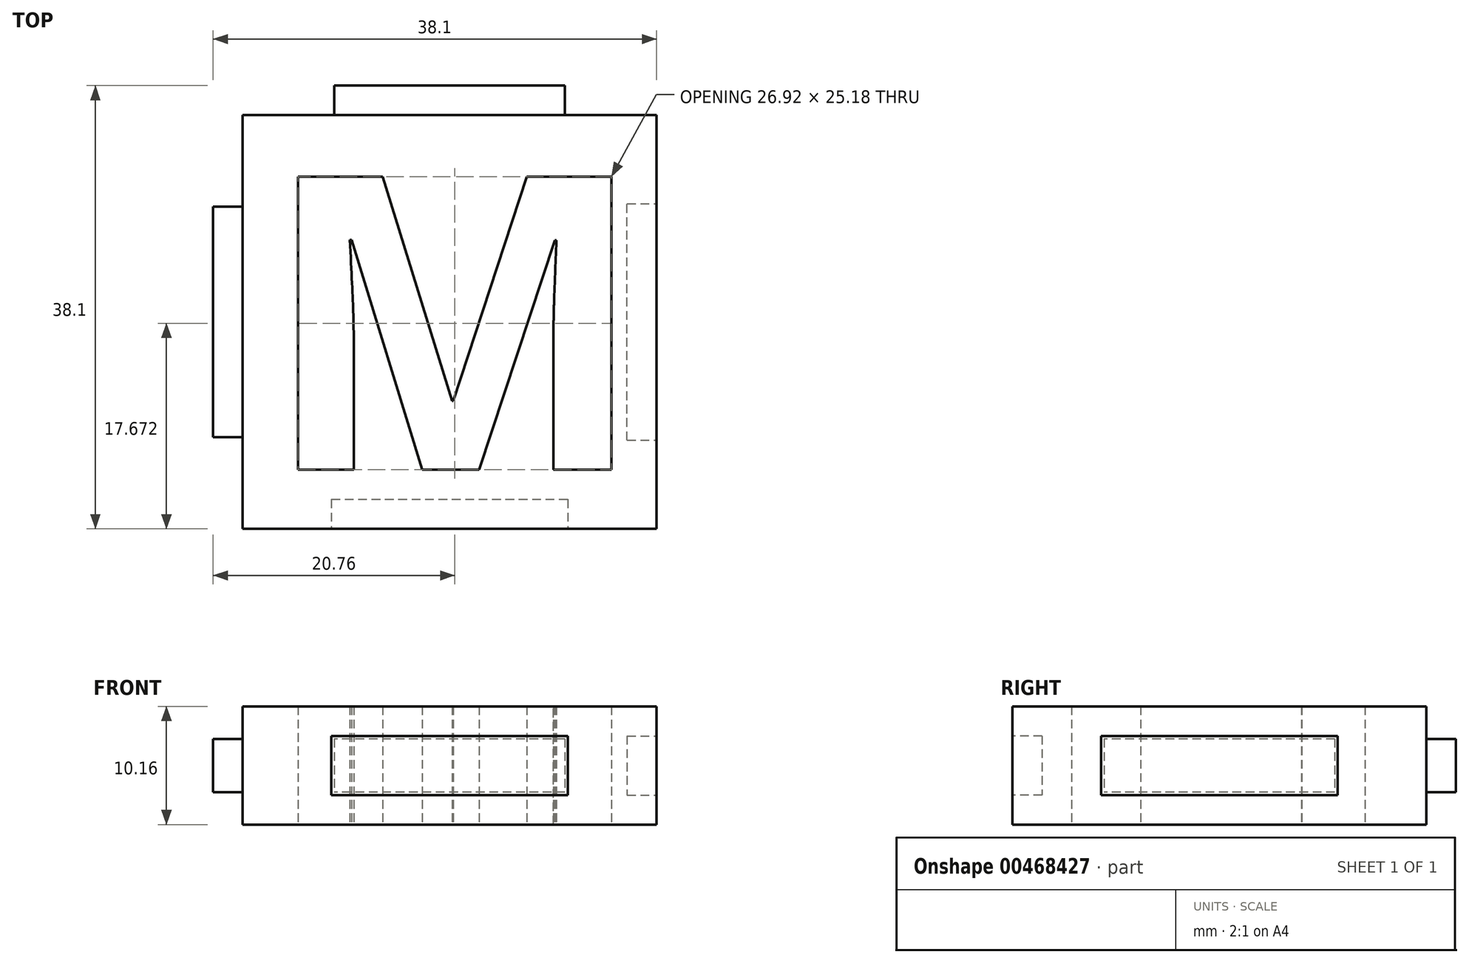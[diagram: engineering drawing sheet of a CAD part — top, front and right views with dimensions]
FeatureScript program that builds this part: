
annotation { "Feature Type Name" : "Feature", "Feature Type Description" : "" }
export const myFeature = defineFeature(function(context is Context, id is Id, definition is map)
    precondition{}
    {
        {
            var Q0;
            Q0=qCreatedBy(makeId("Top.planeOp"),FACE);
            var sketch = newSketch(context, id + "F0", { "sketchPlane" : qUnion([Q0])});
            skLineSegment(sketch, "E0.bottom", {"start": v(-17.78, 17.78) * mm, "end": v(17.78, 17.78) * mm});
            skLineSegment(sketch, "E0.top", {"start": v(-17.78, -17.78) * mm, "end": v(17.78, -17.78) * mm});
            skLineSegment(sketch, "E0.left", {"start": v(-17.78, 17.78) * mm, "end": v(-17.78, -17.78) * mm});
            skLineSegment(sketch, "E0.right", {"start": v(17.78, 17.78) * mm, "end": v(17.78, -17.78) * mm});
            skText(sketch, "E1", { "text": "M", "fontName": "OpenSans-Bold.ttf"});
            const initialGuessF0  = {"E1": [-0.01619, -0.0127, 1, 0, 0.0254]};
            skSetInitialGuess(sketch, initialGuessF0);
            skSolve(sketch);
        }
        {
            var Q0;
            Q0=qSketchRegion(id+"F0",true);
            extrude(context, id + "F1", {"entities" : qUnion([Q0]), "endBound" : BoundingType.SYMMETRIC, "depth" : 10.16 * mm});
        }
        {
            var Q0;
            Q0=makeQuery(id+"F1.opExtrude","SWEPT_FACE",FACE,{"disambiguationData":[OSD([sQuery(id+"F0.wireOp",EDGE,"E0.bottom")])]});
            var sketch = newSketch(context, id + "F2", { "sketchPlane" : qUnion([Q0])});
            skLineSegment(sketch, "E2.bottom", {"start": v(-9.9, 2.29) * mm, "end": v(9.9, 2.29) * mm});
            skLineSegment(sketch, "E2.top", {"start": v(-9.9, -2.29) * mm, "end": v(9.9, -2.29) * mm});
            skLineSegment(sketch, "E2.left", {"start": v(-9.9, 2.29) * mm, "end": v(-9.9, -2.29) * mm});
            skLineSegment(sketch, "E2.right", {"start": v(9.9, 2.29) * mm, "end": v(9.9, -2.29) * mm});
            skSolve(sketch);
        }
        {
            var Q0;
            Q0=qSketchRegion(id+"F2",true);
            extrude(context, id + "F3", {"entities" : qUnion([Q0]), "operationType" : NewBodyOperationType.ADD, "depth" : 2.54 * mm});
        }
        {
            var Q0;
            Q0=makeQuery(id+"F1.opExtrude","SWEPT_FACE",FACE,{"disambiguationData":[OSD([sQuery(id+"F0.wireOp",EDGE,"E0.left")])]});
            var sketch = newSketch(context, id + "F4", { "sketchPlane" : qUnion([Q0])});
            skLineSegment(sketch, "E3.bottom", {"start": v(-9.9, 2.29) * mm, "end": v(9.9, 2.29) * mm});
            skLineSegment(sketch, "E3.top", {"start": v(-9.9, -2.29) * mm, "end": v(9.9, -2.29) * mm});
            skLineSegment(sketch, "E3.left", {"start": v(-9.9, 2.29) * mm, "end": v(-9.9, -2.29) * mm});
            skLineSegment(sketch, "E3.right", {"start": v(9.9, 2.29) * mm, "end": v(9.9, -2.29) * mm});
            skSolve(sketch);
        }
        {
            var Q0;
            Q0=qSketchRegion(id+"F4",true);
            extrude(context, id + "F5", {"entities" : qUnion([Q0]), "operationType" : NewBodyOperationType.ADD, "depth" : 2.54 * mm});
        }
        {
            var Q0;
            Q0=makeQuery(id+"F1.opExtrude","SWEPT_FACE",FACE,{"disambiguationData":[OSD([sQuery(id+"F0.wireOp",EDGE,"E0.top")])]});
            var sketch = newSketch(context, id + "F6", { "sketchPlane" : qUnion([Q0])});
            skLineSegment(sketch, "E4.bottom", {"start": v(-10.16, 2.54) * mm, "end": v(10.16, 2.54) * mm});
            skLineSegment(sketch, "E4.top", {"start": v(-10.16, -2.54) * mm, "end": v(10.16, -2.54) * mm});
            skLineSegment(sketch, "E4.left", {"start": v(-10.16, 2.54) * mm, "end": v(-10.16, -2.54) * mm});
            skLineSegment(sketch, "E4.right", {"start": v(10.16, 2.54) * mm, "end": v(10.16, -2.54) * mm});
            skSolve(sketch);
        }
        {
            var Q0;
            Q0=qSketchRegion(id+"F6",true);
            extrude(context, id + "F7", {"entities" : qUnion([Q0]), "operationType" : NewBodyOperationType.REMOVE, "oppositeDirection" : true, "depth" : 2.54 * mm});
        }
        {
            var Q0;
            Q0=makeQuery(id+"F1.opExtrude","SWEPT_FACE",FACE,{"disambiguationData":[OSD([sQuery(id+"F0.wireOp",EDGE,"E0.right")])]});
            var sketch = newSketch(context, id + "F8", { "sketchPlane" : qUnion([Q0])});
            skLineSegment(sketch, "E5.bottom", {"start": v(-10.16, 2.54) * mm, "end": v(10.16, 2.54) * mm});
            skLineSegment(sketch, "E5.top", {"start": v(-10.16, -2.54) * mm, "end": v(10.16, -2.54) * mm});
            skLineSegment(sketch, "E5.left", {"start": v(-10.16, 2.54) * mm, "end": v(-10.16, -2.54) * mm});
            skLineSegment(sketch, "E5.right", {"start": v(10.16, 2.54) * mm, "end": v(10.16, -2.54) * mm});
            skSolve(sketch);
        }
        {
            var Q0;
            Q0=qSketchRegion(id+"F8",true);
            extrude(context, id + "F9", {"entities" : qUnion([Q0]), "operationType" : NewBodyOperationType.REMOVE, "oppositeDirection" : true, "depth" : 2.54 * mm});
        }
    });
